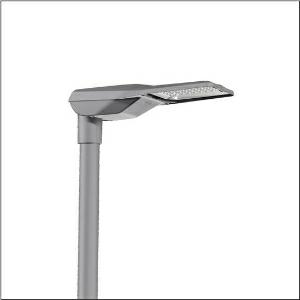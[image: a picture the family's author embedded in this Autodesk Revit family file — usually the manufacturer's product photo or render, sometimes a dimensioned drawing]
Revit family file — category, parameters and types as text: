
# Revit family: streetlight_sl_21_iq_mini___p1_0a_5xe2a31g08hb_5d57
name_source: partatom
category: Lighting Fixtures
units: mm (PartAtom-declared; Revit-internal decimal feet)

## family parameters
Cut with Voids When Loaded = No
Host = Face
Light Source = No
Part Type = Normal
Room Calculation Point = No
Round Connector Dimension = Use Diameter
Shared = No

## types (1)
- --- (1 x LED, 9450 lm, 70.9 W, 3000K)
    Apparent Load = 71 VA
    CIE Flux Codes = 21 50 90 100 100
    Color Rendering = 70
    Color Temperature = 3000K
    Default Elevation = 1800 mm
    Description = Streetlight SL 21 iQ mini, mast luminaire, primary light control with lens, of PMMA, primary optical cover: cover, of toughened safety glass, transparent, light distribution: P1.0a, light emission: direct distribution, primary light characteristic: asymmetric, installation type: post-top, side-entry, LED, High Power LED, rated luminous flux: 9.450lm, luminous efficacy: 133lm/W, light colour: 730, colour temperature: 3000K, control gear: iQ Street-Remote, control: Street-Remote, Auto-Match, Temp-Guard, Lumen-Switch, Night-Set, Smart-Wire, Light-Fading, Desk-Remote (wireless, voltage-free reading and setting of iQ features in the workshop via application-optimized NFC function/RFID function), optimised constant luminous flux control (CLO 2.0), pre-setting: linear dimming characteristic, mains connection: 220..240V, AC, 50/60Hz, start of lifetime: 71W, end of service life: 75W, reduction: 31W, luminaire housing, of diecast aluminium, powder-coated, SITECO metallic grey (DB 702S), corrosivity category C5 high according to DIN EN ISO 12944, please order mast flange separately, inclination adjustable: 0°, 5°, 10°, 15°, sealing non-destructively replaceable, multi-level sealing system, length: 628mm, width: 235mm, height: 110mm, mast flange for spigot size: 42mm (side-entry): 5XC10008XM4, 60/48mm (side-entry/post-top): 5XC10108XM2, 76/60mm (side-entry/post-top): 5XC10108XM1, mounting height: 4..8m, protection rating (complete): IP66, insulation class (complete): insulation class II (safety insulation), certification: CE, ENEC, ENEC+, VDE, impact resistance: IK10, permissible operating ambient temperature for outdoor applications: -40..+50°C, standard-compliant lighting for roads and squares, packaging unit: 1 piece

Light Distribution: P1.0a
    Height = 110 mm
    Lamp = 1 x LED
    Lamp Light Flux = 9450 lm
    Lamp Power = 70.9 W
    Lamp count = 1
    Length = 625 mm
    Luminous efficacy = 133 lm/W
    Manufacturer = Siteco
    ModVariant = No
    Model = 5XE2A31G08HB
    Number of Poles = 1
    OnlyDefault = Yes
    Power Factor = 1
    Product Name = Streetlight SL 21 iQ mini | P1.0a
    Product group = mast luminaire | pylon top
    ProductGroupID = 6100
    Protection Class = Protection class II
    Protection Degree = IP 66
    RLX_Detail_Level = 1
    RLX_Emergency_Light_Flux = 0 lm
    RLX_Emergency_Type = 0
    RLX_Emergency_Type_DB = No
    RlxData = <blob elided: 37473 chars, md5=cc8ac3fb>
    Socket = socket
    Standby Power = 0 W
    System Light Flux = 9450 lm
    System Power = 71 W
    Type Comments = factory setting: luminous flux: 100 % | dim-lin: 254 | 711 mA
    Type Image = l_1003519.jpg
    URL = http://relux.com
    VarID = @adj_157147
    Voltage = 0 V
    Weight = 0.00 kg
    Width = 234 mm

## geometry (parser evidence)
native form markers: Blend x4, Sweep x11
no freeform markers — native parametric forms only
